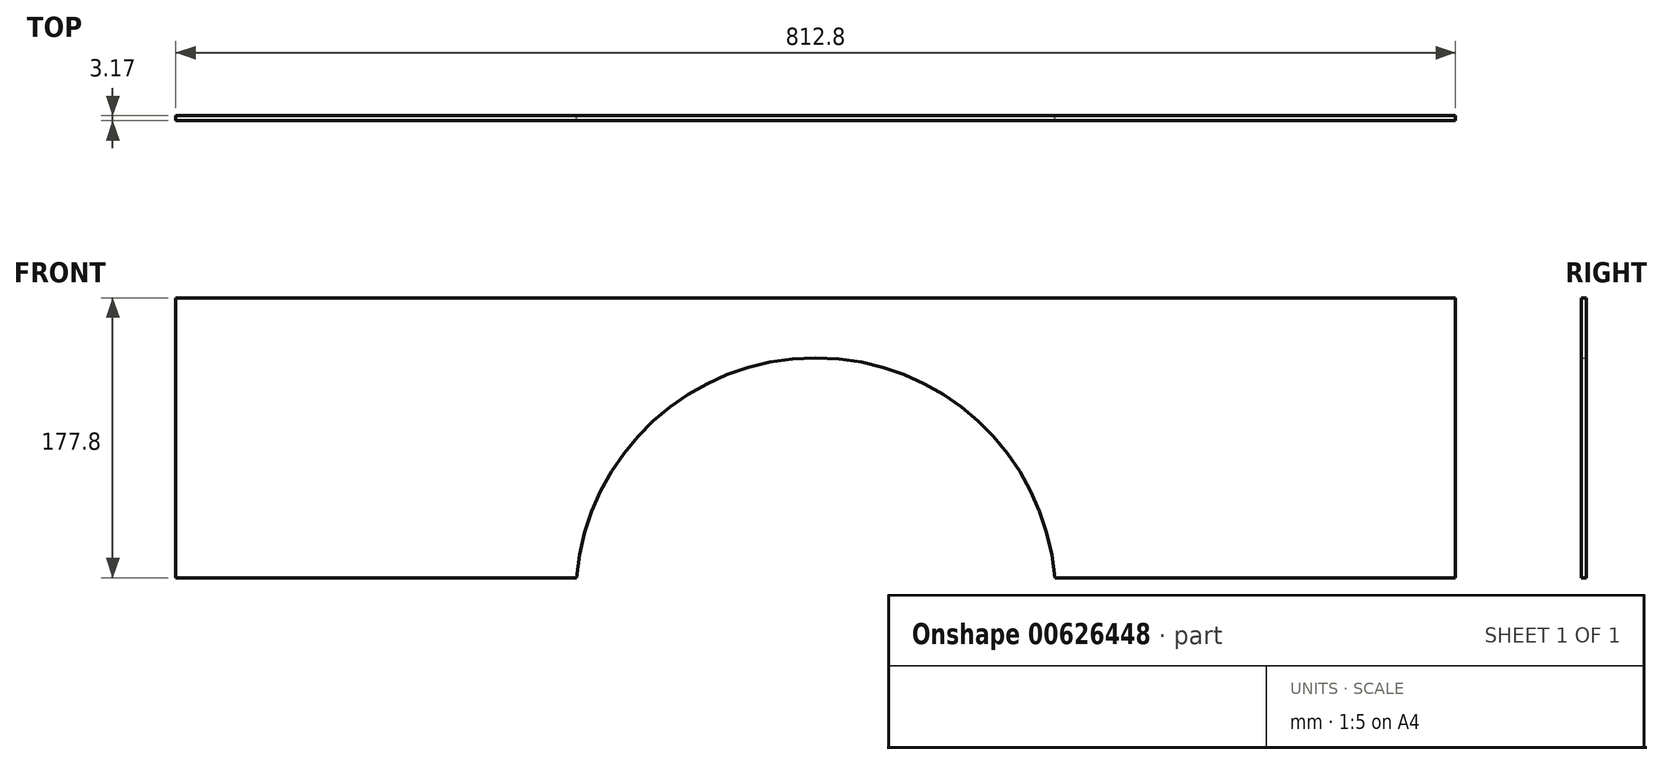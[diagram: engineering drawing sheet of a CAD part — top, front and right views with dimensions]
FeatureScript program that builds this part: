
annotation { "Feature Type Name" : "Feature", "Feature Type Description" : "" }
export const myFeature = defineFeature(function(context is Context, id is Id, definition is map)
    precondition{}
    {
        {
            var Q0;
            Q0=qCreatedBy(makeId("Front.planeOp"),FACE);
            var sketch = newSketch(context, id + "F0", { "sketchPlane" : qUnion([Q0])});
            skLineSegment(sketch, "E0.bottom", {"start": v(0, 0) * mm, "end": v(-812.8, 0) * mm});
            skLineSegment(sketch, "E0.top", {"start": v(0, 177.8) * mm, "end": v(-812.8, 177.8) * mm});
            skLineSegment(sketch, "E0.left", {"start": v(0, 0) * mm, "end": v(0, 177.8) * mm});
            skLineSegment(sketch, "E0.right", {"start": v(-812.8, 0) * mm, "end": v(-812.8, 177.8) * mm});
            skArc(sketch, "E1", {"start": v(-254.53, 0) * mm, "mid": v(-406.4, 139.7) * mm, "end": v(-558.27, 0) * mm});
            skSolve(sketch);
        }
        {
            var Q0;
            Q0=makeQuery(id+"F0.imprint","IMPRINT",FACE,{"disambiguationData":[TD([[makeQuery(id+"F0.imprint","IMPRINT",EDGE,{"derivedFrom":sQuery(id+"F0.wireOp",EDGE,"E0.top")}),1.0]])]});
            extrude(context, id + "F1", {"entities" : qUnion([Q0]), "depth" : 3.17 * mm, "offsetDistance" : 25.4 * mm});
        }
    });
